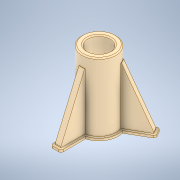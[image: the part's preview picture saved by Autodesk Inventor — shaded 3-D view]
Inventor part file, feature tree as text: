
AUTODESK INVENTOR PART (.ipt)
format: ipt  version: 2021 (Build 250183000, 183)  size: 194,048 bytes
history: native  units: mm
features: extrude x3, sketch x3, chamfer x2, other x1, pattern_circular x1, fillet x1, projected_geometry x1
ambient origin geometry x8: Origin, YZ Plane, XZ Plane, XY Plane, X Axis, Y Axis, Z Axis, Center Point
bodies: Body1 (feature_tree)
feature tree (12):
  other  "Bryła1"
  extrude  "Wyciągnięcie proste1"  Depth=20.0mm
  extrude  "Wyciągnięcie proste2"  Depth=30.0mm
  chamfer  "Faza1"  Distance=60.0mm
  pattern_circular  "Szyk kołowy1"  [2 undecoded]
  extrude  "Wyciągnięcie proste3"  Depth=25.0mm
  fillet  "Zaokrąglenie1"  Radius=50.0mm
  chamfer  "Faza2"  Distance=21.0mm Angle=45.0deg
  sketch  "Szkic1"
  sketch  "Szkic2"
  sketch  "Szkic3"
  projected_geometry  "Pętla rzutowana1"
note: 2 required parameter values undecoded (feature->parameter linkage not recoverable at this tier; creation-order binding heuristic only, values carry confidence <= 0.55)
